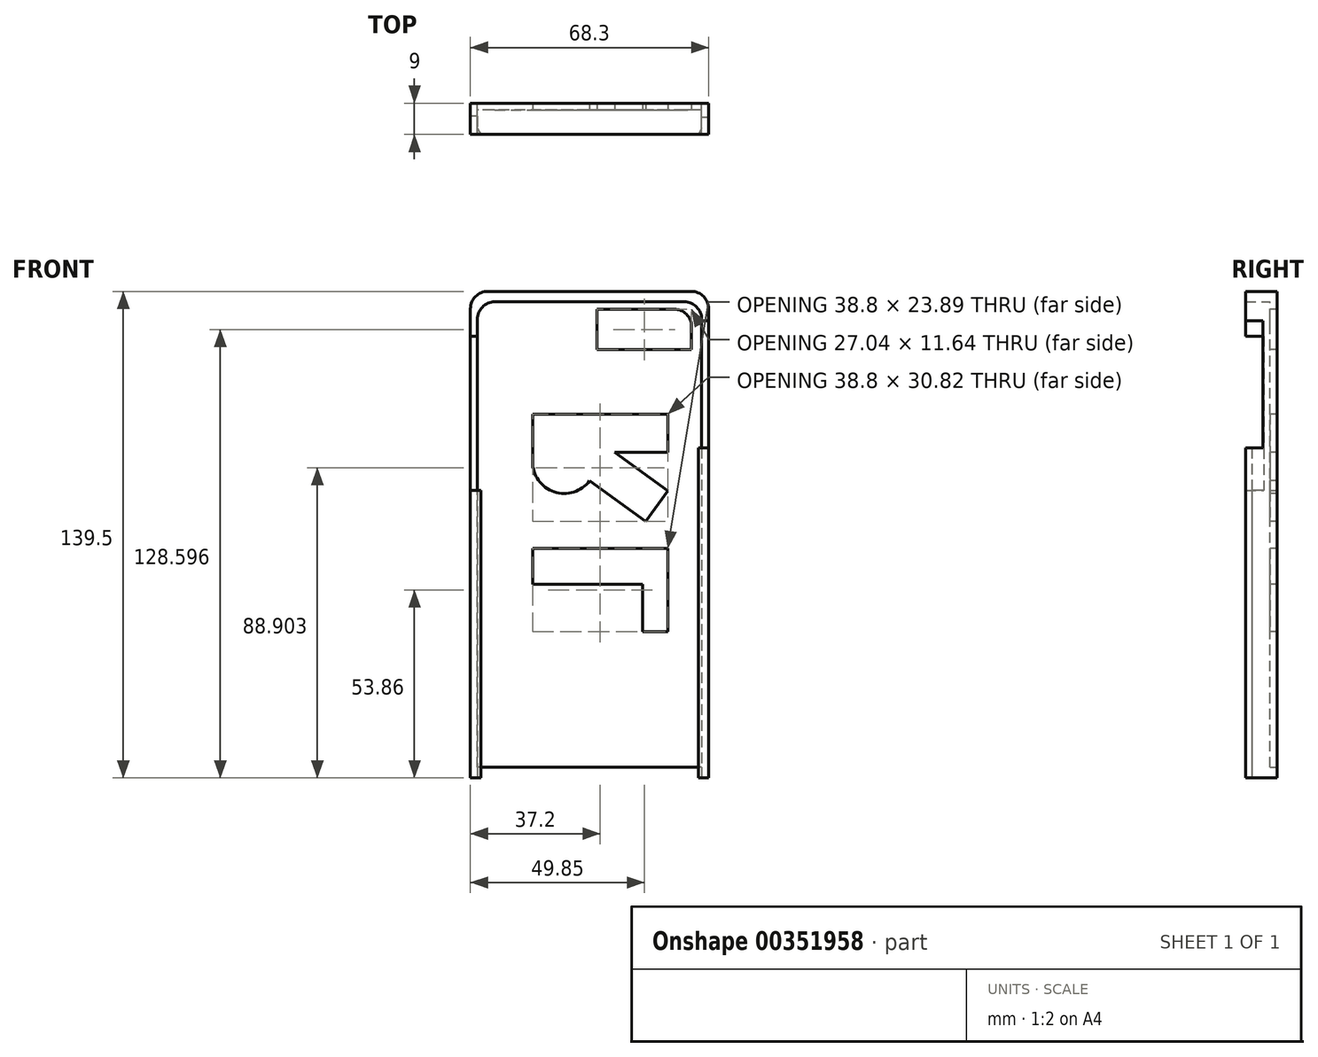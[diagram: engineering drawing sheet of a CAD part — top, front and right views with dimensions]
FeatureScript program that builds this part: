
annotation { "Feature Type Name" : "Feature", "Feature Type Description" : "" }
export const myFeature = defineFeature(function(context is Context, id is Id, definition is map)
    precondition{}
    {
        {
            var Q0;
            Q0=qCreatedBy(makeId("Front.planeOp"),FACE);
            var sketch = newSketch(context, id + "F0", { "sketchPlane" : qUnion([Q0])});
            skLineSegment(sketch, "E0.bottom", {"start": v(34.15, -70.5) * mm, "end": v(-34.15, -70.5) * mm});
            skLineSegment(sketch, "E0.top", {"start": v(29.15, 69) * mm, "end": v(-29.15, 69) * mm});
            skLineSegment(sketch, "E0.left", {"start": v(34.15, -70.5) * mm, "end": v(34.15, 64) * mm});
            skLineSegment(sketch, "E0.right", {"start": v(-34.15, -70.5) * mm, "end": v(-34.15, 64) * mm});
            skPoint(sketch, "E0.middle", {"position": v(0, -0.76) * mm});
            skPoint(sketch, "E1.middle", {"position": v(0, 0) * mm});
            skLineSegment(sketch, "E2", {"start": v(-27.15, 66) * mm, "end": v(27.15, 66) * mm});
            skLineSegment(sketch, "E3", {"start": v(32.15, 61) * mm, "end": v(32.15, -67.5) * mm});
            skLineSegment(sketch, "E4", {"start": v(32.15, -67.5) * mm, "end": v(-32.15, -67.5) * mm});
            skLineSegment(sketch, "E5", {"start": v(-32.15, -67.5) * mm, "end": v(-32.15, 61) * mm});
            skLineSegment(sketch, "E6", {"start": v(-32.15, -67.5) * mm, "end": v(-32.15, -70.5) * mm});
            skLineSegment(sketch, "E7", {"start": v(32.15, -67.5) * mm, "end": v(32.15, -70.5) * mm});
            skPoint(sketch, "E8.visualSharp", {"position": v(-34.15, 69) * mm});
            skArc(sketch, "E8.filletArc", {"start": v(-29.15, 69) * mm, "mid": v(-32.69, 67.53) * mm, "end": v(-34.15, 64) * mm});
            skPoint(sketch, "E9.visualSharp", {"position": v(34.15, 69) * mm});
            skArc(sketch, "E9.filletArc", {"start": v(34.15, 64) * mm, "mid": v(32.69, 67.53) * mm, "end": v(29.15, 69) * mm});
            skPoint(sketch, "E10.visualSharp", {"position": v(-32.15, 66) * mm});
            skArc(sketch, "E10.filletArc", {"start": v(-27.15, 66) * mm, "mid": v(-30.69, 64.53) * mm, "end": v(-32.15, 61) * mm});
            skPoint(sketch, "E11.visualSharp", {"position": v(32.15, 66) * mm});
            skArc(sketch, "E11.filletArc", {"start": v(32.15, 61) * mm, "mid": v(30.69, 64.53) * mm, "end": v(27.15, 66) * mm});
            skSolve(sketch);
        }
        {
            var Q0;
            Q0=makeQuery(id+"F0.imprint","IMPRINT",FACE,{"disambiguationData":[TD([[makeQuery(id+"F0.imprint","IMPRINT",EDGE,{"derivedFrom":sQuery(id+"F0.wireOp",EDGE,"E2")}),-1.0]])]});
            extrude(context, id + "F1", {"entities" : qUnion([Q0]), "depth" : 2 * mm});
        }
        {
            var Q0;
            Q0=makeQuery(id+"F0.imprint","IMPRINT",FACE,{"disambiguationData":[TD([[makeQuery(id+"F0.imprint","IMPRINT",EDGE,{"derivedFrom":sQuery(id+"F0.wireOp",EDGE,"E0.top")}),1.0]])]});
            extrude(context, id + "F2", {"entities" : qUnion([Q0]), "operationType" : NewBodyOperationType.ADD, "depth" : 9 * mm});
        }
        {
            var Q0;
            Q0=makeQuery(id+"F2.opExtrude","SWEPT_FACE",FACE,{"disambiguationData":[OSD([sQuery(id+"F0.wireOp",EDGE,"E0.left")])]});
            var sketch = newSketch(context, id + "F3", { "sketchPlane" : qUnion([Q0])});
            skLineSegment(sketch, "E12.bottom", {"start": v(-9, 24.12) * mm, "end": v(-3.97, 24.12) * mm});
            skLineSegment(sketch, "E12.top", {"start": v(-9, 60.61) * mm, "end": v(-3.97, 60.61) * mm});
            skLineSegment(sketch, "E12.left", {"start": v(-9, 24.12) * mm, "end": v(-9, 60.61) * mm});
            skLineSegment(sketch, "E12.right", {"start": v(-3.97, 24.12) * mm, "end": v(-3.97, 60.61) * mm});
            skSolve(sketch);
        }
        {
            var Q0;
            Q0=makeQuery(id+"F3.imprint","IMPRINT",FACE,{"disambiguationData":[TD([[makeQuery(id+"F3.imprint","IMPRINT",EDGE,{"derivedFrom":sQuery(id+"F3.wireOp",EDGE,"E12.bottom")}),1.0]])]});
            extrude(context, id + "F4", {"entities" : qUnion([Q0]), "operationType" : NewBodyOperationType.REMOVE, "oppositeDirection" : true, "depth" : 5 * mm});
        }
        {
            var Q0;
            Q0=makeQuery(id+"F2.opExtrude","SWEPT_FACE",FACE,{"disambiguationData":[OSD([sQuery(id+"F0.wireOp",EDGE,"E0.right")])]});
            var sketch = newSketch(context, id + "F5", { "sketchPlane" : qUnion([Q0])});
            skLineSegment(sketch, "E13.bottom", {"start": v(9, 11.96) * mm, "end": v(3.77, 11.96) * mm});
            skLineSegment(sketch, "E13.top", {"start": v(9, 56.2) * mm, "end": v(3.77, 56.2) * mm});
            skLineSegment(sketch, "E13.left", {"start": v(9, 11.96) * mm, "end": v(9, 56.2) * mm});
            skLineSegment(sketch, "E13.right", {"start": v(3.77, 11.96) * mm, "end": v(3.77, 56.2) * mm});
            skSolve(sketch);
        }
        {
            var Q0;
            Q0=makeQuery(id+"F5.imprint","IMPRINT",FACE,{"disambiguationData":[TD([[makeQuery(id+"F5.imprint","IMPRINT",EDGE,{"derivedFrom":sQuery(id+"F5.wireOp",EDGE,"E13.bottom")}),-1.0]])]});
            extrude(context, id + "F6", {"entities" : qUnion([Q0]), "operationType" : NewBodyOperationType.REMOVE, "oppositeDirection" : true, "depth" : 5 * mm});
        }
        {
            var Q0;
            Q0=makeQuery(id+"F1.opExtrude","CAP_FACE",FACE,{"disambiguationData":[OSD([sQuery(id+"F0.wireOp",EDGE,"E2"),sQuery(id+"F0.wireOp",EDGE,"E3"),sQuery(id+"F0.wireOp",EDGE,"E4"),sQuery(id+"F0.wireOp",EDGE,"E5"),sQuery(id+"F0.wireOp",EDGE,"E10.filletArc"),sQuery(id+"F0.wireOp",EDGE,"E11.filletArc")])],"isStart":false});
            var sketch = newSketch(context, id + "F7", { "sketchPlane" : qUnion([Q0])});
            skLineSegment(sketch, "E14.bottom", {"start": v(2.18, 52.27) * mm, "end": v(29.22, 52.27) * mm});
            skLineSegment(sketch, "E14.top", {"start": v(2.18, 63.9) * mm, "end": v(24.22, 63.9) * mm});
            skLineSegment(sketch, "E14.left", {"start": v(2.18, 52.27) * mm, "end": v(2.18, 63.9) * mm});
            skLineSegment(sketch, "E14.right", {"start": v(29.22, 52.27) * mm, "end": v(29.22, 58.9) * mm});
            skPoint(sketch, "E15.visualSharp", {"position": v(29.22, 63.9) * mm});
            skArc(sketch, "E15.filletArc", {"start": v(29.22, 58.9) * mm, "mid": v(27.76, 62.44) * mm, "end": v(24.22, 63.9) * mm});
            skSolve(sketch);
        }
        {
            var Q0;
            Q0=makeQuery(id+"F7.imprint","IMPRINT",FACE,{"disambiguationData":[TD([[makeQuery(id+"F7.imprint","IMPRINT",EDGE,{"derivedFrom":sQuery(id+"F7.wireOp",EDGE,"E14.bottom")}),1.0]])]});
            extrude(context, id + "F8", {"entities" : qUnion([Q0]), "operationType" : NewBodyOperationType.REMOVE, "oppositeDirection" : true, "depth" : 10 * mm});
        }
        {
            var Q0;
            Q0=makeQuery(id+"F1.opExtrude","CAP_FACE",FACE,{"disambiguationData":[OSD([sQuery(id+"F0.wireOp",EDGE,"E2"),sQuery(id+"F0.wireOp",EDGE,"E3"),sQuery(id+"F0.wireOp",EDGE,"E4"),sQuery(id+"F0.wireOp",EDGE,"E5"),sQuery(id+"F0.wireOp",EDGE,"E10.filletArc"),sQuery(id+"F0.wireOp",EDGE,"E11.filletArc")])],"isStart":false});
            var sketch = newSketch(context, id + "F9", { "sketchPlane" : qUnion([Q0])});
            skLineSegment(sketch, "E16", {"start": v(-16.35, 33.8) * mm, "end": v(22.45, 33.8) * mm});
            skLineSegment(sketch, "E17", {"start": v(22.45, 33.8) * mm, "end": v(22.45, 22.88) * mm});
            skLineSegment(sketch, "E18", {"start": v(22.45, 22.88) * mm, "end": v(7.24, 22.88) * mm});
            skLineSegment(sketch, "E19", {"start": v(7.24, 22.88) * mm, "end": v(22.45, 11.77) * mm});
            skLineSegment(sketch, "E20", {"start": v(22.45, 11.77) * mm, "end": v(16.03, 2.98) * mm});
            skLineSegment(sketch, "E21", {"start": v(16.03, 2.98) * mm, "end": v(0, 14.7) * mm});
            skLineSegment(sketch, "E22", {"start": v(-16.35, 33.8) * mm, "end": v(-16.35, 20.15) * mm});
            skArc(sketch, "E23", {"start": v(-16.35, 20.15) * mm, "mid": v(-10.14, 11.54) * mm, "end": v(0, 14.7) * mm});
            skCircle(sketch, "E24", {"center": v(-7.38, 24.05) * mm, "radius": 5.07 * mm});
            skLineSegment(sketch, "E25", {"start": v(-16.35, -4.7) * mm, "end": v(-16.35, -14.94) * mm});
            skLineSegment(sketch, "E26", {"start": v(22.45, -4.7) * mm, "end": v(-16.35, -4.7) * mm});
            skLineSegment(sketch, "E27", {"start": v(-16.35, -14.94) * mm, "end": v(15.24, -14.94) * mm});
            skLineSegment(sketch, "E28", {"start": v(15.24, -14.94) * mm, "end": v(15.24, -28.6) * mm});
            skLineSegment(sketch, "E29", {"start": v(15.24, -28.6) * mm, "end": v(22.45, -28.6) * mm});
            skLineSegment(sketch, "E30", {"start": v(22.45, -28.6) * mm, "end": v(22.45, -4.7) * mm});
            skPoint(sketch, "E31.orphan", {"position": v(22.45, -43.22) * mm});
            skLineSegment(sketch, "E32.trimOffspring", {"start": v(22.45, -4.7) * mm, "end": v(22.45, -28.6) * mm});
            skSolve(sketch);
        }
        {
            var Q0;
            Q0=makeQuery(id+"F9.imprint","IMPRINT",FACE,{"disambiguationData":[TD([[makeQuery(id+"F9.imprint","IMPRINT",EDGE,{"derivedFrom":sQuery(id+"F9.wireOp",EDGE,"E26")}),1.0]])]});
            var Q1;
            Q1=makeQuery(id+"F9.imprint","IMPRINT",FACE,{"disambiguationData":[TD([[makeQuery(id+"F9.imprint","IMPRINT",EDGE,{"derivedFrom":sQuery(id+"F9.wireOp",EDGE,"E16")}),-1.0]])]});
            var Q2;
            Q2=makeQuery(id+"F9.imprint","IMPRINT",FACE,{"disambiguationData":[TD([[makeQuery(id+"F9.imprint","IMPRINT",EDGE,{"derivedFrom":sQuery(id+"F9.wireOp",EDGE,"E24")}),1.0]])]});
            extrude(context, id + "F10", {"entities" : qUnion([Q0, Q1, Q2]), "operationType" : NewBodyOperationType.REMOVE, "oppositeDirection" : true, "depth" : 25 * mm});
        }
        {
            var Q0;
            Q0=makeQuery(id+"F2.opExtrude","SWEPT_FACE",FACE,{"disambiguationData":[OSD([sQuery(id+"F0.wireOp",EDGE,"E3"),sQuery(id+"F0.wireOp",EDGE,"E7")])]});
            var sketch = newSketch(context, id + "F11", { "sketchPlane" : qUnion([Q0])});
            skLineSegment(sketch, "E33.bottom", {"start": v(9, 24.12) * mm, "end": v(7.18, 24.12) * mm});
            skLineSegment(sketch, "E33.top", {"start": v(9, -70.5) * mm, "end": v(7.18, -70.5) * mm});
            skLineSegment(sketch, "E33.left", {"start": v(9, 24.12) * mm, "end": v(9, -70.5) * mm});
            skLineSegment(sketch, "E33.right", {"start": v(7.18, 24.12) * mm, "end": v(7.18, -70.5) * mm});
            skSolve(sketch);
        }
        {
            var Q0;
            Q0=makeQuery(id+"F11.imprint","IMPRINT",FACE,{"disambiguationData":[TD([[makeQuery(id+"F11.imprint","IMPRINT",EDGE,{"derivedFrom":sQuery(id+"F11.wireOp",EDGE,"E33.bottom")}),1.0]])]});
            extrude(context, id + "F12", {"entities" : qUnion([Q0]), "operationType" : NewBodyOperationType.ADD, "depth" : 1 * mm});
        }
        {
            var Q0;
            Q0=makeQuery(id+"F2.opExtrude","SWEPT_FACE",FACE,{"disambiguationData":[OSD([sQuery(id+"F0.wireOp",EDGE,"E5"),sQuery(id+"F0.wireOp",EDGE,"E6")])]});
            var sketch = newSketch(context, id + "F13", { "sketchPlane" : qUnion([Q0])});
            skLineSegment(sketch, "E34.bottom", {"start": v(-9, 11.96) * mm, "end": v(-7.18, 11.96) * mm});
            skLineSegment(sketch, "E34.top", {"start": v(-9, -70.5) * mm, "end": v(-7.18, -70.5) * mm});
            skLineSegment(sketch, "E34.left", {"start": v(-9, 11.96) * mm, "end": v(-9, -70.5) * mm});
            skLineSegment(sketch, "E34.right", {"start": v(-7.18, 11.96) * mm, "end": v(-7.18, -70.5) * mm});
            skSolve(sketch);
        }
        {
            var Q0;
            Q0=makeQuery(id+"F13.imprint","IMPRINT",FACE,{"disambiguationData":[TD([[makeQuery(id+"F13.imprint","IMPRINT",EDGE,{"derivedFrom":sQuery(id+"F13.wireOp",EDGE,"E34.bottom")}),1.0]])]});
            extrude(context, id + "F14", {"entities" : qUnion([Q0]), "operationType" : NewBodyOperationType.ADD, "depth" : 1 * mm});
        }
        {
            var Q0;
            {var subQ0=sQuery(id+"F0.wireOp",EDGE,"E0.bottom");Q0=makeQuery(id+"F12.boolean.opBoolean","MERGE",FACE,{"derivedFrom":[makeQuery(id+"F2.opExtrude","SWEPT_FACE",FACE,{"disambiguationData":[OSD([subQ0]),TDD([makeQuery(id+"F0.imprint","IMPRINT",EDGE,{"disambiguationData":[TD([[makeQuery(id+"F0.imprint","INTERSECT",VERTEX,{"derivedFrom":[subQ0,sQuery(id+"F0.wireOp",EDGE,"E0.left")]}),-1.0]])],"derivedFrom":subQ0})])]}),makeQuery(id+"F12.opExtrude","SWEPT_FACE",FACE,{"disambiguationData":[OSD([sQuery(id+"F11.wireOp",EDGE,"E33.top")])]})]});}
            var sketch = newSketch(context, id + "F15", { "sketchPlane" : qUnion([Q0])});
            skLineSegment(sketch, "E35", {"start": v(32.15, 7.18) * mm, "end": v(31.15, 9) * mm});
            skSolve(sketch);
        }
        {
            var Q0;
            Q0=makeQuery(id+"F15.imprint","IMPRINT",FACE,{"disambiguationData":[TD([[makeQuery(id+"F15.imprint","IMPRINT",EDGE,{"derivedFrom":sQuery(id+"F15.wireOp",EDGE,"E35")}),1.0]])]});
            extrude(context, id + "F16", {"entities" : qUnion([Q0]), "operationType" : NewBodyOperationType.REMOVE, "oppositeDirection" : true, "depth" : 95 * mm});
        }
        {
            var Q0;
            {var subQ0=sQuery(id+"F0.wireOp",EDGE,"E0.bottom");Q0=makeQuery(id+"F14.boolean.opBoolean","MERGE",FACE,{"derivedFrom":[makeQuery(id+"F2.opExtrude","SWEPT_FACE",FACE,{"disambiguationData":[OSD([subQ0]),TDD([makeQuery(id+"F0.imprint","IMPRINT",EDGE,{"disambiguationData":[TD([[makeQuery(id+"F0.imprint","INTERSECT",VERTEX,{"derivedFrom":[subQ0,sQuery(id+"F0.wireOp",EDGE,"E0.right")]}),1.0]])],"derivedFrom":subQ0})])]}),makeQuery(id+"F14.opExtrude","SWEPT_FACE",FACE,{"disambiguationData":[OSD([sQuery(id+"F13.wireOp",EDGE,"E34.top")])]})]});}
            var sketch = newSketch(context, id + "F17", { "sketchPlane" : qUnion([Q0])});
            skLineSegment(sketch, "E36", {"start": v(-32.15, 7.18) * mm, "end": v(-31.15, 9) * mm});
            skSolve(sketch);
        }
        {
            var Q0;
            Q0=makeQuery(id+"F17.imprint","IMPRINT",FACE,{"disambiguationData":[TD([[makeQuery(id+"F17.imprint","IMPRINT",EDGE,{"derivedFrom":sQuery(id+"F17.wireOp",EDGE,"E36")}),-1.0]])]});
            extrude(context, id + "F18", {"entities" : qUnion([Q0]), "operationType" : NewBodyOperationType.REMOVE, "oppositeDirection" : true, "depth" : 85 * mm});
        }
    });
